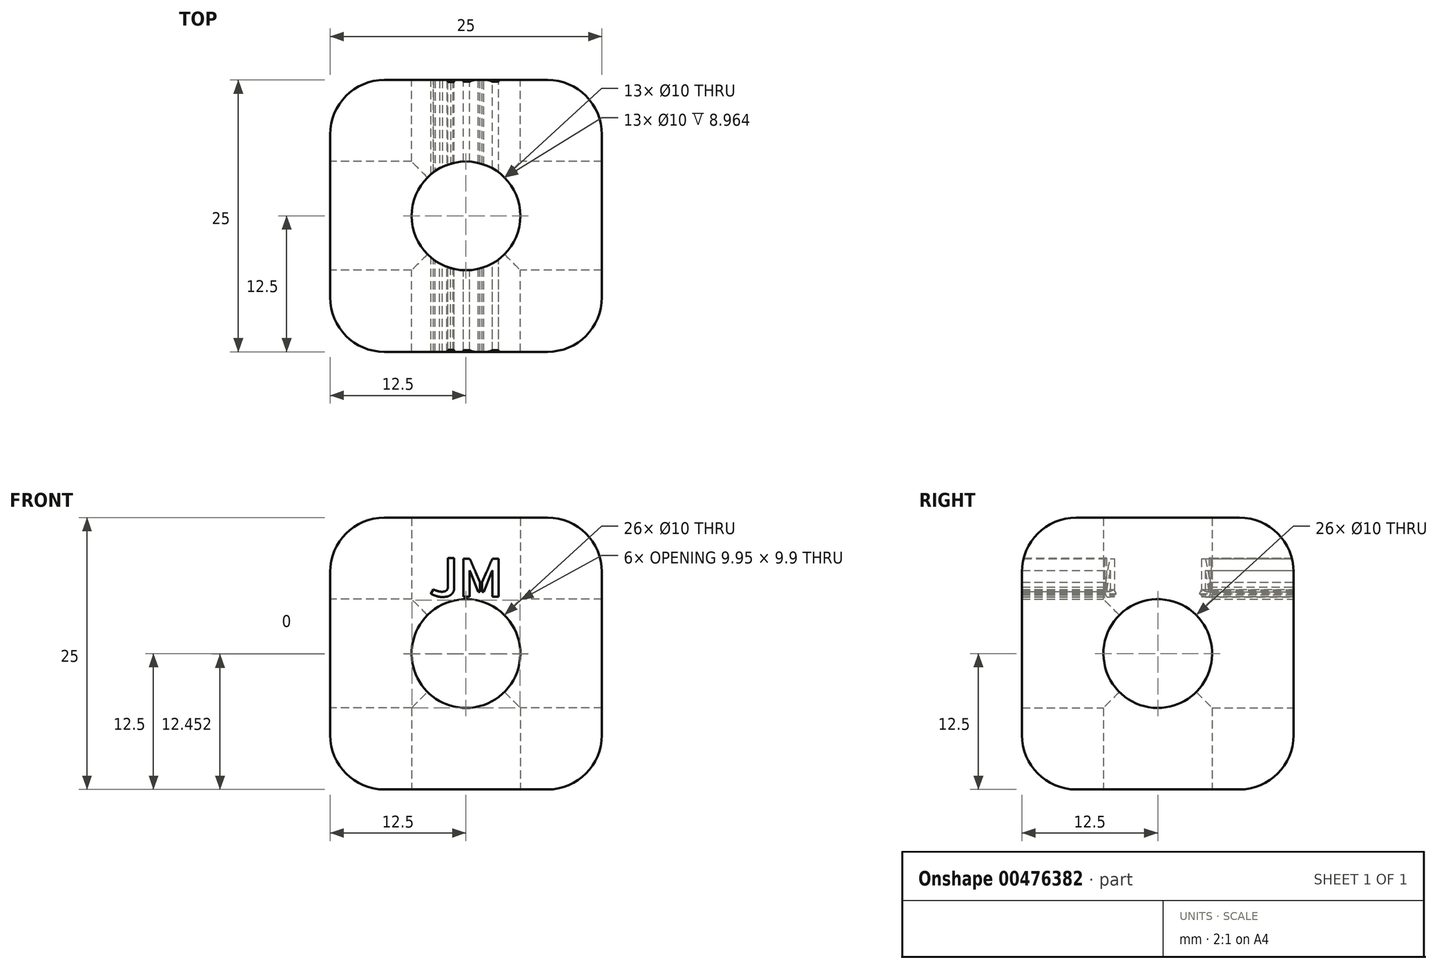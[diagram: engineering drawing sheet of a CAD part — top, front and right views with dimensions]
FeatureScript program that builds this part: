
annotation { "Feature Type Name" : "Feature", "Feature Type Description" : "" }
export const myFeature = defineFeature(function(context is Context, id is Id, definition is map)
    precondition{}
    {
        {
            var Q0;
            Q0=qCreatedBy(makeId("Front.planeOp"),FACE);
            var sketch = newSketch(context, id + "F0", { "sketchPlane" : qUnion([Q0])});
            skLineSegment(sketch, "E0.bottom", {"start": v(12.5, 12.5) * mm, "end": v(-12.5, 12.5) * mm});
            skLineSegment(sketch, "E0.top", {"start": v(12.5, -12.5) * mm, "end": v(-12.5, -12.5) * mm});
            skLineSegment(sketch, "E0.left", {"start": v(12.5, 12.5) * mm, "end": v(12.5, -12.5) * mm});
            skLineSegment(sketch, "E0.right", {"start": v(-12.5, 12.5) * mm, "end": v(-12.5, -12.5) * mm});
            skPoint(sketch, "E0.middle", {"position": v(0, 0) * mm});
            skSolve(sketch);
        }
        {
            var Q0;
            Q0=makeQuery(id+"F0.imprint","IMPRINT",FACE,{"disambiguationData":[TD([[makeQuery(id+"F0.imprint","IMPRINT",EDGE,{"derivedFrom":sQuery(id+"F0.wireOp",EDGE,"E0.bottom")}),1.0]])]});
            extrude(context, id + "F1", {"entities" : qUnion([Q0]), "depth" : 25 * mm});
        }
        {
            var Q0;
            Q0=makeQuery(id+"F1.opExtrude","CAP_EDGE",EDGE,{"disambiguationData":[OSD([sQuery(id+"F0.wireOp",EDGE,"E0.right")])],"isStart":false});
            var Q1;
            Q1=makeQuery(id+"F1.opExtrude","CAP_EDGE",EDGE,{"disambiguationData":[OSD([sQuery(id+"F0.wireOp",EDGE,"E0.bottom")])],"isStart":false});
            var Q2;
            Q2=makeQuery(id+"F1.opExtrude","CAP_EDGE",EDGE,{"disambiguationData":[OSD([sQuery(id+"F0.wireOp",EDGE,"E0.left")])],"isStart":false});
            var Q3;
            Q3=makeQuery(id+"F1.opExtrude","CAP_EDGE",EDGE,{"disambiguationData":[OSD([sQuery(id+"F0.wireOp",EDGE,"E0.top")])],"isStart":false});
            var Q4;
            Q4=makeQuery(id+"F1.opExtrude","SWEPT_EDGE",EDGE,{"disambiguationData":[OSD([sQuery(id+"F0.wireOp",EDGE,"E0.top"),sQuery(id+"F0.wireOp",EDGE,"E0.left")])]});
            var Q5;
            Q5=makeQuery(id+"F1.opExtrude","SWEPT_EDGE",EDGE,{"disambiguationData":[OSD([sQuery(id+"F0.wireOp",EDGE,"E0.bottom"),sQuery(id+"F0.wireOp",EDGE,"E0.left")])]});
            var Q6;
            Q6=makeQuery(id+"F1.opExtrude","CAP_EDGE",EDGE,{"disambiguationData":[OSD([sQuery(id+"F0.wireOp",EDGE,"E0.left")])],"isStart":true});
            var Q7;
            Q7=makeQuery(id+"F1.opExtrude","SWEPT_EDGE",EDGE,{"disambiguationData":[OSD([sQuery(id+"F0.wireOp",EDGE,"E0.top"),sQuery(id+"F0.wireOp",EDGE,"E0.right")])]});
            var Q8;
            Q8=makeQuery(id+"F1.opExtrude","SWEPT_FACE",FACE,{"disambiguationData":[OSD([sQuery(id+"F0.wireOp",EDGE,"E0.top")])]});
            var Q9;
            Q9=makeQuery(id+"F1.opExtrude","CAP_EDGE",EDGE,{"disambiguationData":[OSD([sQuery(id+"F0.wireOp",EDGE,"E0.bottom")])],"isStart":true});
            var Q10;
            Q10=makeQuery(id+"F1.opExtrude","CAP_EDGE",EDGE,{"disambiguationData":[OSD([sQuery(id+"F0.wireOp",EDGE,"E0.right")])],"isStart":true});
            var Q11;
            Q11=makeQuery(id+"F1.opExtrude","SWEPT_EDGE",EDGE,{"disambiguationData":[OSD([sQuery(id+"F0.wireOp",EDGE,"E0.bottom"),sQuery(id+"F0.wireOp",EDGE,"E0.right")])]});
            fillet(context, id + "F2", {"entities" : qUnion([Q0, Q1, Q2, Q3, Q4, Q5, Q6, Q7, Q8, Q9, Q10, Q11]), "radius" : 5 * mm, "tangentPropagation" : true, "allowEdgeOverflow" : false});
        }
        {
            var Q0;
            Q0=qCreatedBy(makeId("Front.planeOp"),FACE);
            var sketch = newSketch(context, id + "F3", { "sketchPlane" : qUnion([Q0])});
            skCircle(sketch, "E1", {"center": v(0, 0) * mm, "radius": 5 * mm});
            skSolve(sketch);
        }
        {
            var Q0;
            Q0=sQuery(id+"F3.wireOp",VERTEX,"E1.center");
            var Q1;
            Q1=makeQuery(id+"F1.opExtrude","SWEPT_BODY",BODY,{"disambiguationData":[OSD([sQuery(id+"F0.wireOp",EDGE,"E0.bottom"),sQuery(id+"F0.wireOp",EDGE,"E0.top"),sQuery(id+"F0.wireOp",EDGE,"E0.left"),sQuery(id+"F0.wireOp",EDGE,"E0.right")])]});
            hole(context, id + "F4", {"style" : HoleStyle.SIMPLE, "endStyle" : HoleEndStyle.THROUGH, "oppositeDirection" : true, "holeDiameter" : 10 * mm, "isTappedThrough" : true, "tappedDepth" : 12 * mm, "tapClearance" : 3, "locations" : qUnion([Q0]), "scope" : qUnion([Q1])});
        }
        {
            var Q0;
            Q0=makeQuery(id+"F1.opExtrude","SWEPT_FACE",FACE,{"disambiguationData":[OSD([sQuery(id+"F0.wireOp",EDGE,"E0.top")])]});
            var sketch = newSketch(context, id + "F5", { "sketchPlane" : qUnion([Q0])});
            skCircle(sketch, "E2", {"center": v(0, 12.5) * mm, "radius": 5 * mm});
            skPoint(sketch, "E2.centerSnap0", {"position": v(-7.5, 12.5) * mm});
            skSolve(sketch);
        }
        {
            var Q0;
            Q0=sQuery(id+"F5.wireOp",VERTEX,"E2.center");
            var Q1;
            Q1=makeQuery(id+"F1.opExtrude","SWEPT_BODY",BODY,{"disambiguationData":[OSD([sQuery(id+"F0.wireOp",EDGE,"E0.bottom"),sQuery(id+"F0.wireOp",EDGE,"E0.top"),sQuery(id+"F0.wireOp",EDGE,"E0.left"),sQuery(id+"F0.wireOp",EDGE,"E0.right")])]});
            hole(context, id + "F6", {"style" : HoleStyle.SIMPLE, "endStyle" : HoleEndStyle.THROUGH, "holeDiameter" : 10 * mm, "isTappedThrough" : true, "tappedDepth" : 12 * mm, "tapClearance" : 3, "locations" : qUnion([Q0]), "scope" : qUnion([Q1])});
        }
        {
            var Q0;
            Q0=makeQuery(id+"F1.opExtrude","SWEPT_FACE",FACE,{"disambiguationData":[OSD([sQuery(id+"F0.wireOp",EDGE,"E0.right")])]});
            var sketch = newSketch(context, id + "F7", { "sketchPlane" : qUnion([Q0])});
            skCircle(sketch, "E3", {"center": v(12.5, 0) * mm, "radius": 5 * mm});
            skPoint(sketch, "E3.centerSnap0", {"position": v(12.5, 7.5) * mm});
            skSolve(sketch);
        }
        {
            var Q0;
            Q0=sQuery(id+"F7.wireOp",VERTEX,"E3.center");
            var Q1;
            Q1=makeQuery(id+"F1.opExtrude","SWEPT_BODY",BODY,{"disambiguationData":[OSD([sQuery(id+"F0.wireOp",EDGE,"E0.bottom"),sQuery(id+"F0.wireOp",EDGE,"E0.top"),sQuery(id+"F0.wireOp",EDGE,"E0.left"),sQuery(id+"F0.wireOp",EDGE,"E0.right")])]});
            hole(context, id + "F8", {"style" : HoleStyle.SIMPLE, "endStyle" : HoleEndStyle.THROUGH, "holeDiameter" : 10 * mm, "isTappedThrough" : true, "tappedDepth" : 12 * mm, "tapClearance" : 3, "locations" : qUnion([Q0]), "scope" : qUnion([Q1])});
        }
        {
            var Q0;
            Q0=qCreatedBy(makeId("Front.planeOp"),FACE);
            var sketch = newSketch(context, id + "F9", { "sketchPlane" : qUnion([Q0])});
            skText(sketch, "E4", { "text": "JM", "fontName": "AllertaStencil-Regular.ttf"});
            const initialGuessF9  = {"E4": [-0.00335, 0.00522, 1, 0, 0.0035]};
            skSetInitialGuess(sketch, initialGuessF9);
            skSolve(sketch);
        }
        {
            var Q0;
            Q0 = qSketchRegion(id + "F9", true);
            extrude(context, id + "F10", {"entities" : qUnion([Q0]), "operationType" : NewBodyOperationType.REMOVE, "endBound" : BoundingType.THROUGH_ALL, "depth" : 25 * mm});
        }
    });
